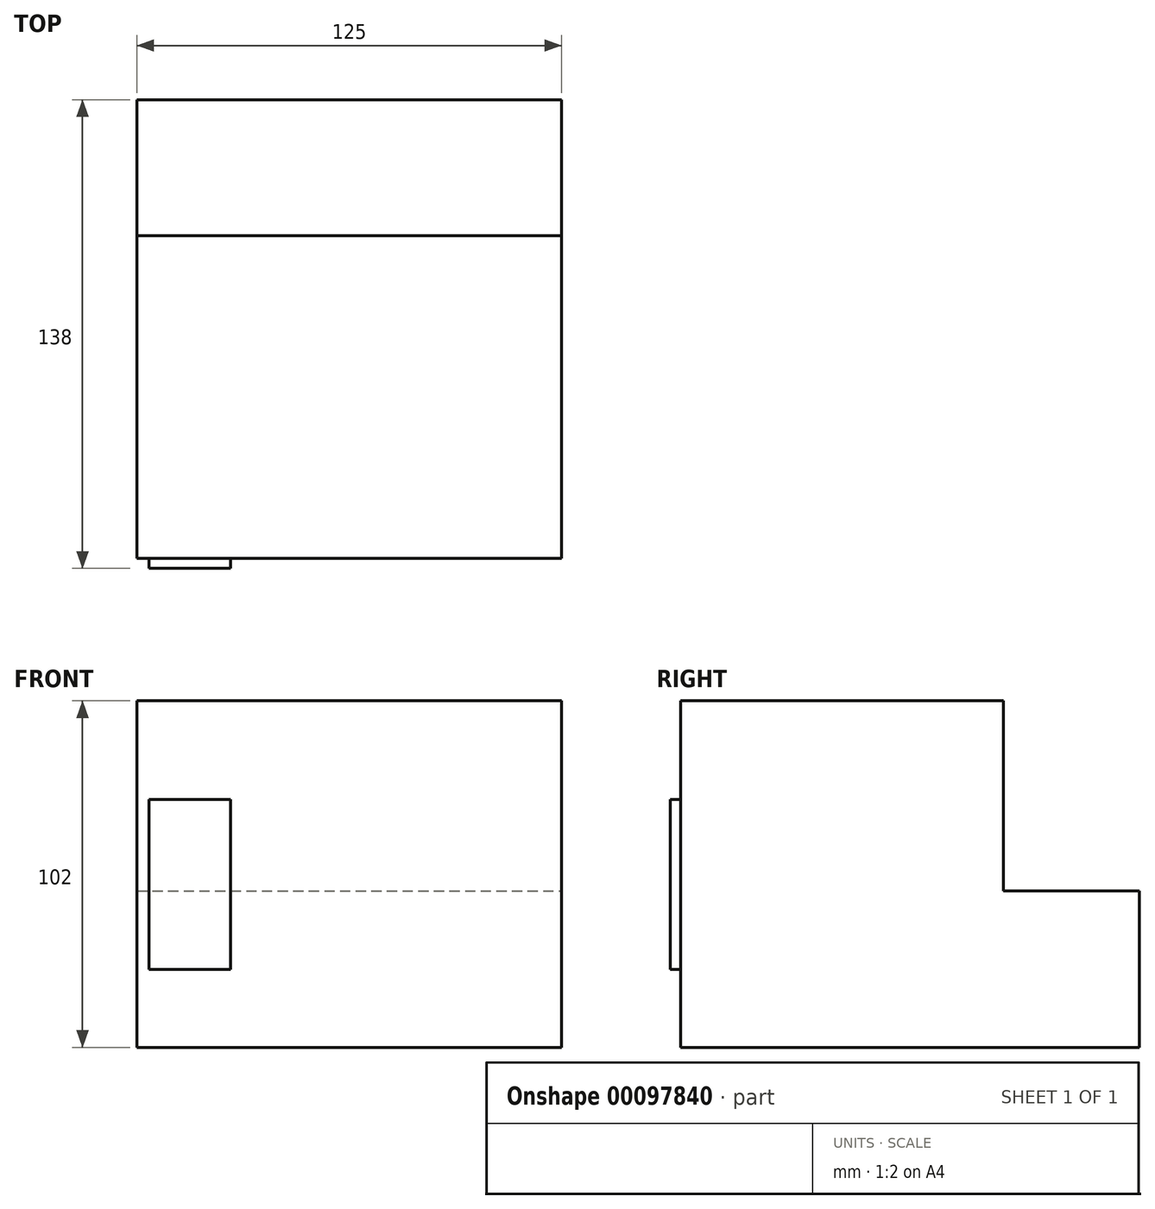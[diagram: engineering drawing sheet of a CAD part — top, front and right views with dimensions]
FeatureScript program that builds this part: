
annotation { "Feature Type Name" : "Feature", "Feature Type Description" : "" }
export const myFeature = defineFeature(function(context is Context, id is Id, definition is map)
    precondition{}
    {
        {
            var Q0;
            Q0=qCreatedBy(makeId("Top.planeOp"),FACE);
            var sketch = newSketch(context, id + "F0", { "sketchPlane" : qUnion([Q0])});
            skLineSegment(sketch, "E0.bottom", {"start": v(0, 0) * mm, "end": v(125, 0) * mm});
            skLineSegment(sketch, "E0.top", {"start": v(0, 135) * mm, "end": v(125, 135) * mm});
            skLineSegment(sketch, "E0.left", {"start": v(0, 0) * mm, "end": v(0, 135) * mm});
            skLineSegment(sketch, "E0.right", {"start": v(125, 0) * mm, "end": v(125, 135) * mm});
            skLineSegment(sketch, "E1", {"start": v(0, 95) * mm, "end": v(125, 95) * mm});
            skSolve(sketch);
        }
        {
            var Q0;
            Q0 = qSketchRegion(id + "F0", true);
            var Q1;
            Q1=makeQuery(id+"F0.imprint","IMPRINT",FACE,{"disambiguationData":[TD([[makeQuery(id+"F0.imprint","IMPRINT",EDGE,{"derivedFrom":sQuery(id+"F0.wireOp",EDGE,"E0.bottom")}),1.0]])]});
            extrude(context, id + "F1", {"entities" : qUnion([Q0, Q1]), "depth" : 102 * mm});
        }
        {
            var Q0;
            {var subQ0=sQuery(id+"F0.wireOp",EDGE,"E0.top");Q0=makeQuery(id+"F0.imprint","IMPRINT",FACE,{"disambiguationData":[TD([[makeQuery(id+"F0.imprint","IMPRINT",EDGE,{"derivedFrom":subQ0}),-1.0]])]});}
            extrude(context, id + "F2", {"entities" : qUnion([Q0]), "operationType" : NewBodyOperationType.REMOVE, "depth" : 132.07 * mm, "hasSecondDirection" : true, "secondDirectionOppositeDirection" : false, "secondDirectionDepth" : 46 * mm});
        }
        {
            var Q0;
            Q0=makeQuery(id+"F1.opExtrude","SWEPT_FACE",FACE,{"disambiguationData":[OSD([sQuery(id+"F0.wireOp",EDGE,"E0.bottom")])]});
            var sketch = newSketch(context, id + "F3", { "sketchPlane" : qUnion([Q0])});
            skLineSegment(sketch, "E2.bottom", {"start": v(3.6, 73) * mm, "end": v(27.6, 73) * mm});
            skLineSegment(sketch, "E2.top", {"start": v(3.6, 23) * mm, "end": v(27.6, 23) * mm});
            skLineSegment(sketch, "E2.left", {"start": v(3.6, 73) * mm, "end": v(3.6, 23) * mm});
            skLineSegment(sketch, "E2.right", {"start": v(27.6, 73) * mm, "end": v(27.6, 23) * mm});
            skLineSegment(sketch, "E3", {"start": v(52.64, 95) * mm, "end": v(98.96, 95) * mm});
            skLineSegment(sketch, "E4", {"start": v(98.96, 95) * mm, "end": v(121, 65.28) * mm});
            skLineSegment(sketch, "E5", {"start": v(121, 65.28) * mm, "end": v(121, 27.36) * mm});
            skLineSegment(sketch, "E6", {"start": v(121, 27.36) * mm, "end": v(98.96, 7) * mm});
            skLineSegment(sketch, "E7", {"start": v(98.96, 7) * mm, "end": v(52.64, 7) * mm});
            skLineSegment(sketch, "E8", {"start": v(52.64, 7) * mm, "end": v(30.6, 27.36) * mm});
            skLineSegment(sketch, "E9", {"start": v(30.6, 27.36) * mm, "end": v(30.6, 65.28) * mm});
            skLineSegment(sketch, "E10", {"start": v(30.6, 65.28) * mm, "end": v(52.64, 95) * mm});
            skSolve(sketch);
        }
        {
            var Q0;
            Q0=makeQuery(id+"F3.imprint","IMPRINT",FACE,{"disambiguationData":[TD([[makeQuery(id+"F3.imprint","IMPRINT",EDGE,{"derivedFrom":sQuery(id+"F3.wireOp",EDGE,"E2.bottom")}),-1.0]])]});
            extrude(context, id + "F4", {"entities" : qUnion([Q0]), "operationType" : NewBodyOperationType.ADD, "depth" : 3 * mm});
        }
    });
